# Revit family: Difusores abiertos para pasillos entre estanterías
name_source: partatom
category: Rociadores
revit_build: Autodesk Revit 2017 (Build: 20160225_1515(x64)
units: mm (PartAtom-declared; Revit-internal decimal feet)

## family parameters
Compartido = No
Corte con vacíos al cargar = No
Cota de conector redondo = Radio de uso
Mantener orientación de anotación = No
Número OmniClass = 23.65.70.17.11.24
Punto de cálculo de habitación = No
Se basa en plano de trabajo = Sí
Siempre vertical = Sí
Tipo de pieza = Normal
Título OmniClass = Fire Fighting Sprinkler Heads

## types (2) — shared parameters
Clase de presión = Norma
Cobertura = Norma
Descripción = Cabeza  nebulizadora abierta para instalación en tubería seca, fabricada en acero inoxidable AISI304 para alta presión.
Equipada con 3 ó 5 toberas  en línea en un ángulo de 180º para una cobertura de 4 m lineales y 1,5 m de ancho.
Elevación por defecto = 1219 mm
Fabricante = Aguilera Electrónica
Orificio = Norma
Respuesta = Norma
Simbolo texto modelo = Sí
Símbolo = Sí
URL = http://aguilera.es
Zona de acción = Sí

## per-type parameters (varying)
| type | 5 toberas | Flujo | Flujo máximo | Flujo mínimo | Modelo |
| Difusor abierto 5 toberas - 2,0 a 25,5 l/min | Sí | 2.0 L/min | 25.5 L/min | 2.0 L/min | AN/CA180T5 |
| Difusor abierto 3 toberas - 1,2 a 15,3 l/min | No | 1.2 L/min | 15.3 L/min | 1.2 L/min | AN/CA180T3 |
